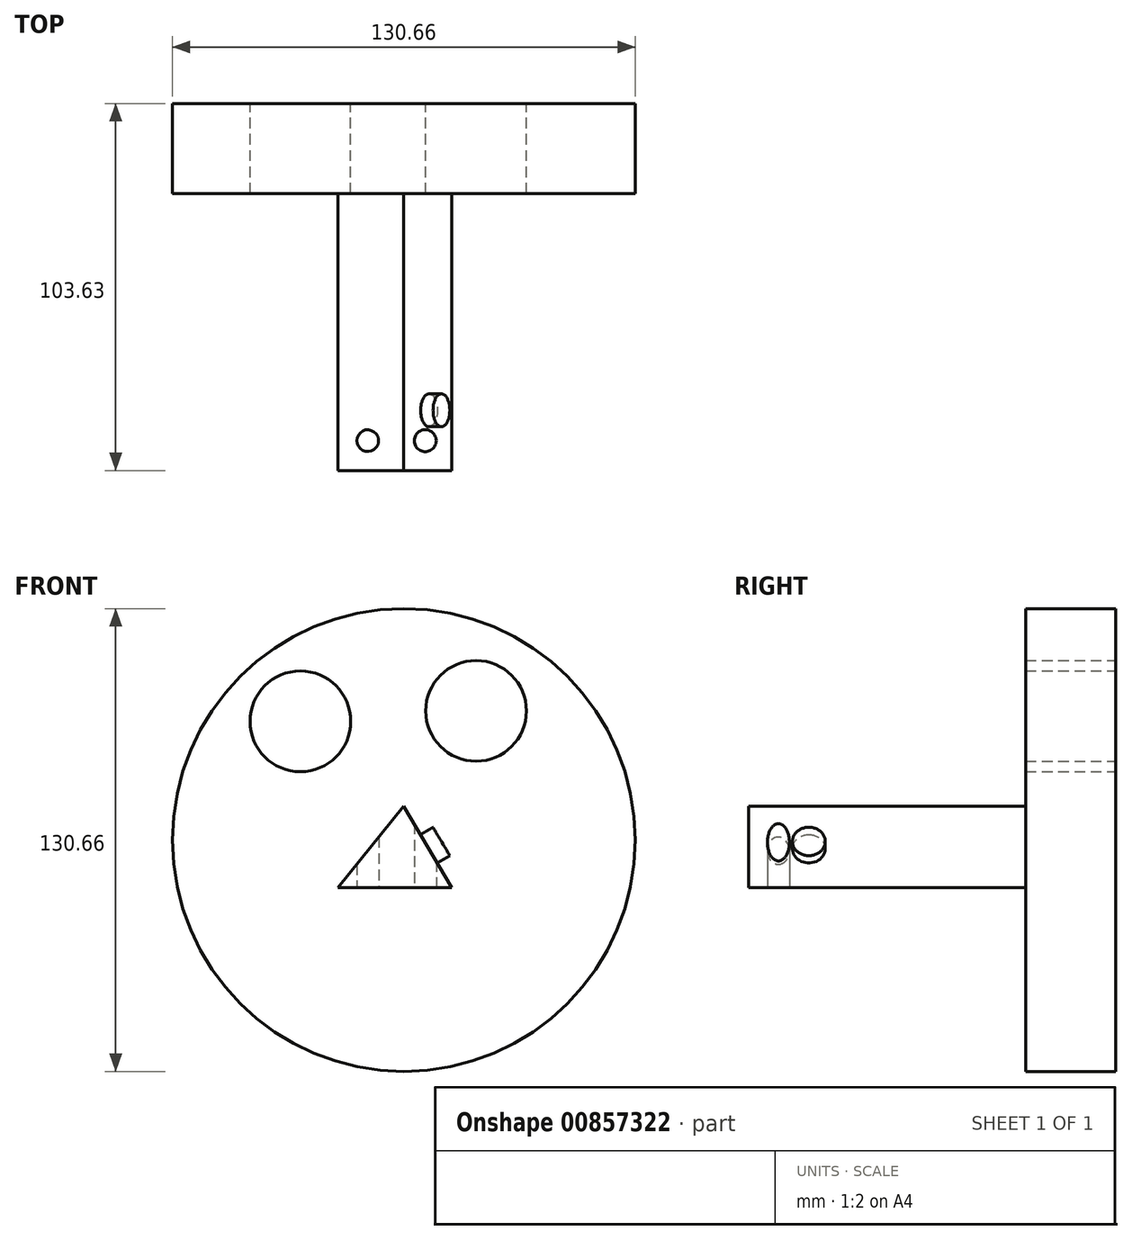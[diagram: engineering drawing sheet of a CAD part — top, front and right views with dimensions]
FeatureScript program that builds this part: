
annotation { "Feature Type Name" : "Feature", "Feature Type Description" : "" }
export const myFeature = defineFeature(function(context is Context, id is Id, definition is map)
    precondition{}
    {
        {
            var Q0;
            Q0=qCreatedBy(makeId("Front.planeOp"),FACE);
            var sketch = newSketch(context, id + "F0", { "sketchPlane" : qUnion([Q0])});
            skCircle(sketch, "E0", {"center": v(0, 0) * mm, "radius": 65.33 * mm});
            skCircle(sketch, "E1", {"center": v(-29.2, 33.5) * mm, "radius": 14.22 * mm});
            skCircle(sketch, "E2", {"center": v(20.4, 36.46) * mm, "radius": 14.22 * mm});
            skSolve(sketch);
        }
        {
            var Q0;
            Q0 = qSketchRegion(id + "F0", true);
            extrude(context, id + "F1", {"entities" : qUnion([Q0]), "depth" : 25.4 * mm, "offsetDistance" : 25.4 * mm});
        }
        {
            var Q0;
            Q0=makeQuery(id+"F1.opExtrude","CAP_FACE",FACE,{"disambiguationData":[OSD([sQuery(id+"F0.wireOp",EDGE,"E0"),sQuery(id+"F0.wireOp",EDGE,"E1"),sQuery(id+"F0.wireOp",EDGE,"E2")])],"isStart":false});
            var sketch = newSketch(context, id + "F2", { "sketchPlane" : qUnion([Q0])});
            skLineSegment(sketch, "E3", {"start": v(0, 9.61) * mm, "end": v(-18.57, -13.4) * mm});
            skLineSegment(sketch, "E4", {"start": v(-18.57, -13.4) * mm, "end": v(13.55, -13.4) * mm});
            skLineSegment(sketch, "E5", {"start": v(13.55, -13.4) * mm, "end": v(0, 9.61) * mm});
            skSolve(sketch);
        }
        {
            var Q0;
            Q0 = qSketchRegion(id + "F2", true);
            extrude(context, id + "F3", {"entities" : qUnion([Q0]), "operationType" : NewBodyOperationType.ADD, "depth" : 78.23 * mm, "offsetDistance" : 25.4 * mm});
        }
        {
            var Q0;
            Q0=makeQuery(id+"F3.opExtrude","SWEPT_FACE",FACE,{"disambiguationData":[OSD([sQuery(id+"F2.wireOp",EDGE,"E5")])]});
            var sketch = newSketch(context, id + "F4", { "sketchPlane" : qUnion([Q0])});
            skCircle(sketch, "E6", {"center": v(-86.61, -5.72) * mm, "radius": 4.64 * mm});
            skSolve(sketch);
        }
        {
            var Q0;
            Q0 = qSketchRegion(id + "F4", true);
            extrude(context, id + "F5", {"entities" : qUnion([Q0]), "operationType" : NewBodyOperationType.ADD, "depth" : 4.06 * mm, "offsetDistance" : 25.4 * mm});
        }
        {
            var Q0;
            Q0=makeQuery(id+"F3.opExtrude","SWEPT_FACE",FACE,{"disambiguationData":[OSD([sQuery(id+"F2.wireOp",EDGE,"E4")])]});
            var sketch = newSketch(context, id + "F6", { "sketchPlane" : qUnion([Q0])});
            skCircle(sketch, "E7", {"center": v(-10.18, 95.2) * mm, "radius": 3.1 * mm});
            skCircle(sketch, "E8", {"center": v(6.04, 95.2) * mm, "radius": 3.1 * mm});
            skSolve(sketch);
        }
        {
            var Q0;
            Q0 = qSketchRegion(id + "F6", true);
            extrude(context, id + "F7", {"entities" : qUnion([Q0]), "operationType" : NewBodyOperationType.REMOVE, "oppositeDirection" : true, "depth" : 28.96 * mm, "offsetDistance" : 25.4 * mm});
        }
    });
